# Revit family: 19 inches modular drawers to be equipped with cassettes
name_source: partatom
category: Installations électriques
units: mm (PartAtom-declared; Revit-internal decimal feet)

## family parameters
Basée sur le plan de construction = Non
Conserver l'orientation des annotations = Non
Cote de connecteur circulaire = Utiliser le diamètre
Couper avec des vides une fois chargée = Non
Partagée = Non
Point de calcul de pièce = Non
Toujours verticalement = Oui
Type d'élément = Normal

## types (3) — shared parameters
E-catalogue link = https://www.legrand.fr
ETIM class = EC001130
Function = 19 inches modular optic drawer to be equipped with fibre optic blocks
IK = IK05
Mounting method = 19 inches housing
Operating temperature = -30°C à 60°C
Pre-wired = Non
Storage temperature = -30°C à 60°C
Width (mm) = 483 mm
With front plate = Non
With housing = Non
With pigtails = Non
zero-valued in all types: Elévation par défaut

## per-type parameters (varying)
| type | Depth | EAN | Front management | Front management type | Height | Legrand part number | Number of height units | Rear management | With label holder |
| 19 inches modular drawer HD 1U to be equipped | 201 mm  [stored 0.659449 ft] | 3414971929173 | Non | Front management : 2U | 44 mm  [stored 0.144357 ft] | 032175 | 1 | Non | Non |
| 19 inches modular drawer HD 2U to be equipped | 492 mm  [stored 1.61417 ft] | 3414971929180 | Oui | Front management : 2U | 89 mm  [stored 0.291995 ft] | 032176 | 2 | Oui | Oui |
| 19 inches modular drawer HD 4U to be equipped | 492 mm  [stored 1.61417 ft] | 3414971929197 | Oui | Front management : 4U | 178 mm  [stored 0.58399 ft] | 032177 | 4 | Oui | Oui |

note: column(s) folded — value = type name in every type: BIM wording

note: [stored X ft] marks values corroborated as IEEE doubles in the binary element streams (Revit-internal decimal feet)
